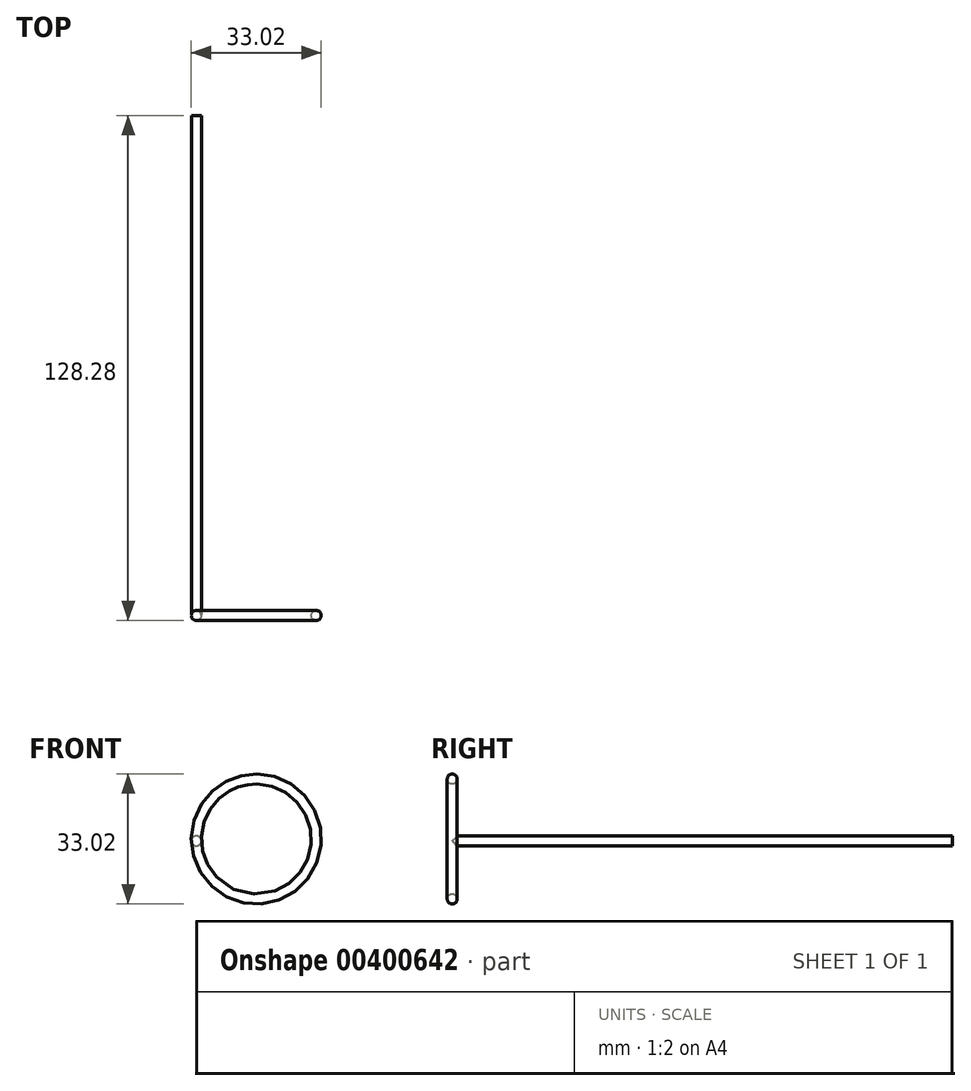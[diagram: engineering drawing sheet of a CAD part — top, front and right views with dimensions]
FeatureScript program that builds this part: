
annotation { "Feature Type Name" : "Feature", "Feature Type Description" : "" }
export const myFeature = defineFeature(function(context is Context, id is Id, definition is map)
    precondition{}
    {
        {
            var Q0;
            Q0=qCreatedBy(makeId("Front.planeOp"),FACE);
            var sketch = newSketch(context, id + "F0", { "sketchPlane" : qUnion([Q0])});
            skCircle(sketch, "E0", {"center": v(0, 0) * mm, "radius": 1.27 * mm});
            skSolve(sketch);
        }
        {
            var Q0;
            Q0=qCreatedBy(makeId("Top.planeOp"),FACE);
            var sketch = newSketch(context, id + "F1", { "sketchPlane" : qUnion([Q0])});
            skLineSegment(sketch, "E1", {"start": v(0, 0) * mm, "end": v(0, -127) * mm});
            skSolve(sketch);
        }
        {
            var Q0;
            Q0=makeQuery(id+"F0.imprint","IMPRINT",FACE,{"disambiguationData":[TD([[makeQuery(id+"F0.imprint","IMPRINT",EDGE,{"derivedFrom":sQuery(id+"F0.wireOp",EDGE,"E0")}),1.0]])]});
            var Q1;
            Q1=sQuery(id+"F1.wireOp",EDGE,"E1");
            sweep(context, id + "F2", {"profiles" : qUnion([Q0]), "path" : qUnion([Q1])});
        }
        {
            var Q0;
            Q0=qCreatedBy(makeId("Front.planeOp"),FACE);
            cPlane(context, id + "F3", {"entities" : qUnion([Q0]), "cplaneType" : CPlaneType.OFFSET, "offset" : 127 * mm, "width" : 152.4 * mm, "height" : 152.4 * mm});
        }
        {
            var Q0;
            Q0=qCreatedBy(id+"F3.planeOp",FACE);
            var sketch = newSketch(context, id + "F4", { "sketchPlane" : qUnion([Q0])});
            skCircle(sketch, "E2", {"center": v(15.23, 0.5) * mm, "radius": 15.24 * mm});
            skPoint(sketch, "E2.first.point", {"position": v(0, 0) * mm});
            skPoint(sketch, "E2.second.point", {"position": v(30.46, 0) * mm});
            skPoint(sketch, "E2.third.point", {"position": v(30.3, 2.8) * mm});
            skSolve(sketch);
        }
        {
            var Q0;
            Q0=qCreatedBy(makeId("Top.planeOp"),FACE);
            var sketch = newSketch(context, id + "F5", { "sketchPlane" : qUnion([Q0])});
            skCircle(sketch, "E3", {"center": v(0, -127.01) * mm, "radius": 1.27 * mm});
            skSolve(sketch);
        }
        {
            var Q0;
            Q0=makeQuery(id+"F5.imprint","IMPRINT",FACE,{"disambiguationData":[TD([[makeQuery(id+"F5.imprint","IMPRINT",EDGE,{"derivedFrom":sQuery(id+"F5.wireOp",EDGE,"E3")}),1.0]])]});
            var Q1;
            Q1=sQuery(id+"F4.wireOp",EDGE,"E2");
            sweep(context, id + "F6", {"operationType" : NewBodyOperationType.ADD, "profiles" : qUnion([Q0]), "path" : qUnion([Q1])});
        }
    });
